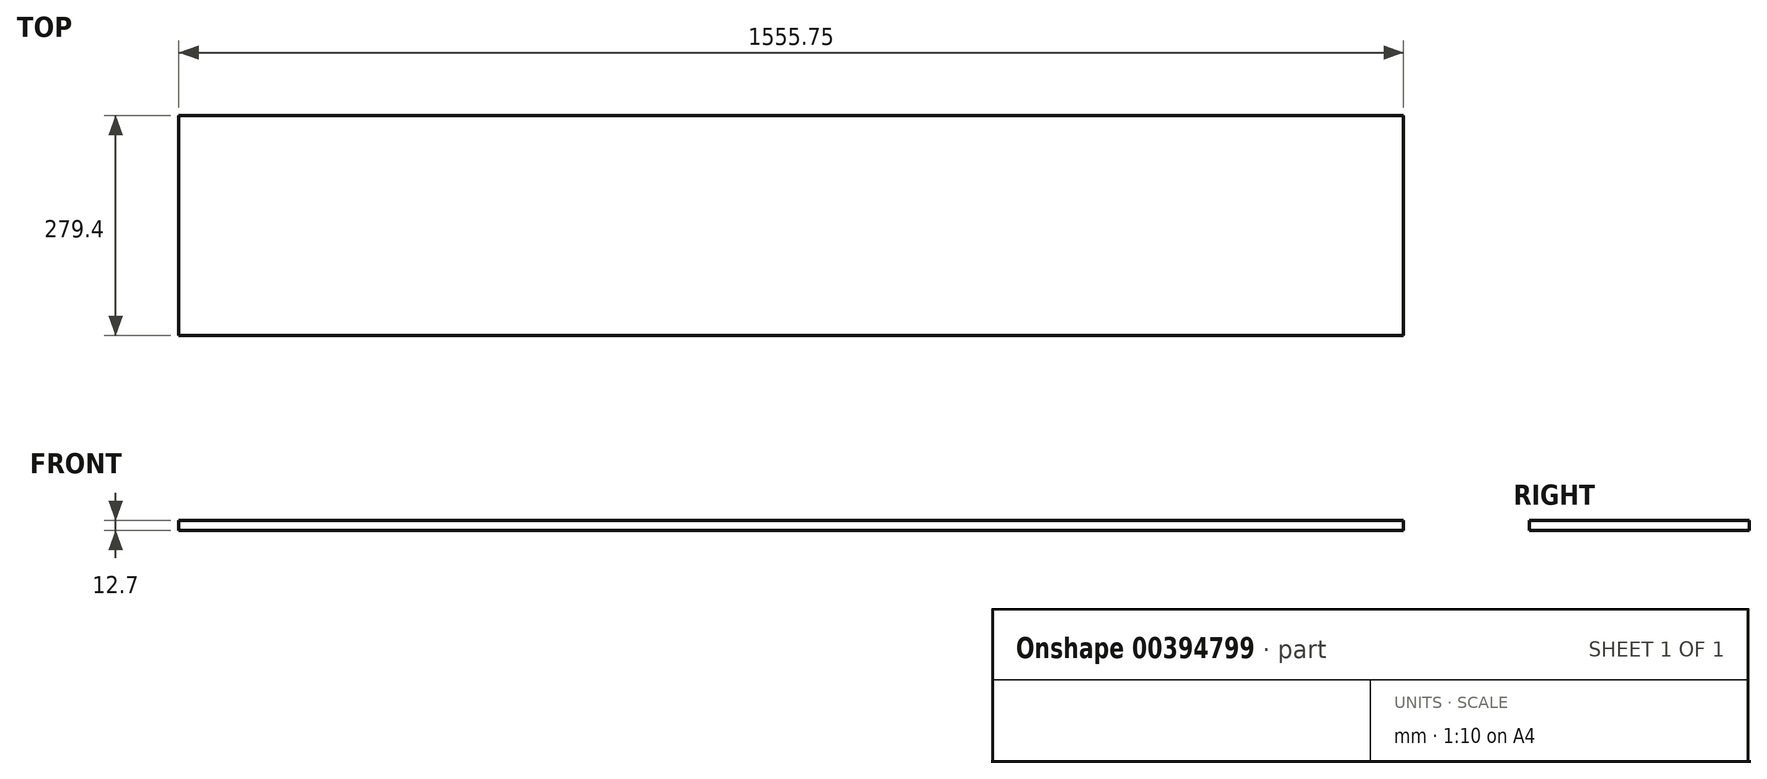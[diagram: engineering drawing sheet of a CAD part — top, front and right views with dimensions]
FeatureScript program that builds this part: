
annotation { "Feature Type Name" : "Feature", "Feature Type Description" : "" }
export const myFeature = defineFeature(function(context is Context, id is Id, definition is map)
    precondition{}
    {
        {
            var Q0;
            Q0=qCreatedBy(makeId("Top.planeOp"),FACE);
            var sketch = newSketch(context, id + "F0", { "sketchPlane" : qUnion([Q0])});
            skLineSegment(sketch, "E0.bottom", {"start": v(-245.13, 126.02) * mm, "end": v(1310.62, 126.02) * mm});
            skLineSegment(sketch, "E0.top", {"start": v(-245.13, -153.38) * mm, "end": v(1310.62, -153.38) * mm});
            skLineSegment(sketch, "E0.left", {"start": v(-245.13, 126.02) * mm, "end": v(-245.13, -153.38) * mm});
            skLineSegment(sketch, "E0.right", {"start": v(1310.62, 126.02) * mm, "end": v(1310.62, -153.38) * mm});
            skSolve(sketch);
        }
        {
            var Q0;
            Q0 = qSketchRegion(id + "F0", true);
            extrude(context, id + "F1", {"entities" : qUnion([Q0]), "depth" : 12.7 * mm});
        }
    });
